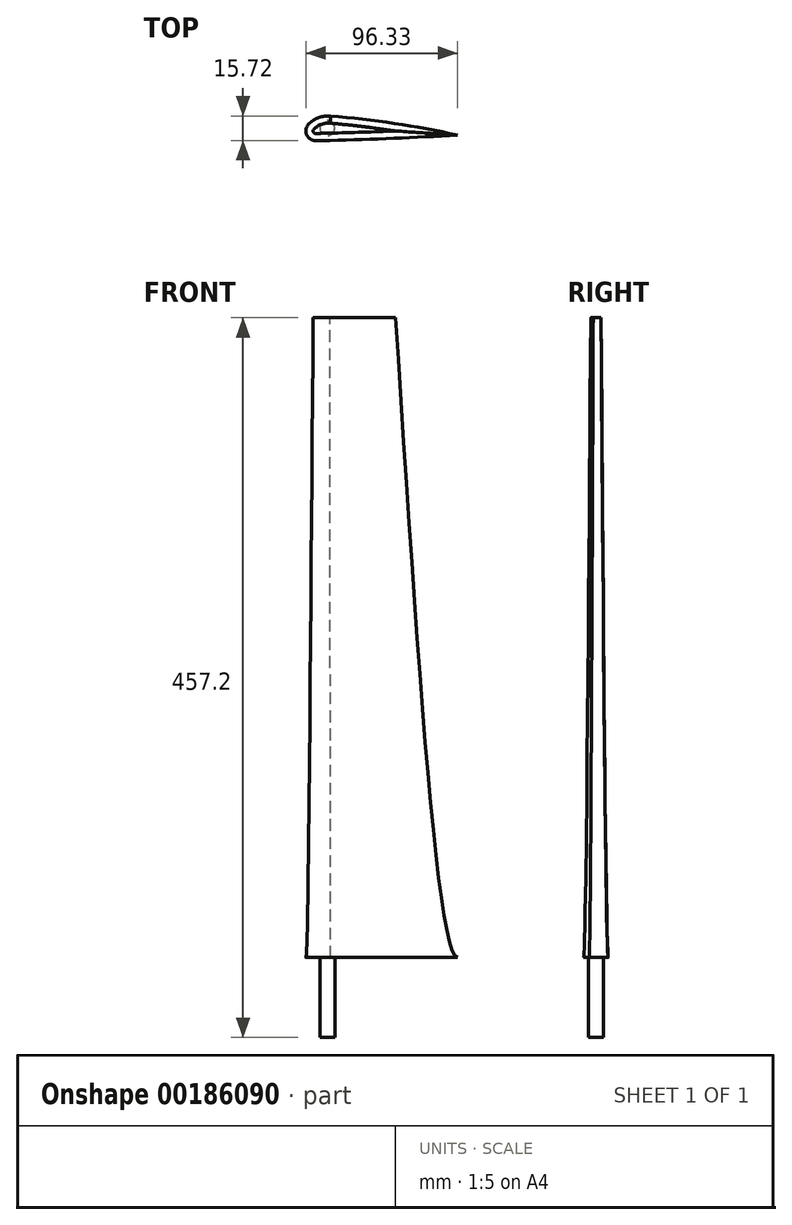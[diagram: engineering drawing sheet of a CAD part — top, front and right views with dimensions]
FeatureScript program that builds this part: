
annotation { "Feature Type Name" : "Feature", "Feature Type Description" : "" }
export const myFeature = defineFeature(function(context is Context, id is Id, definition is map)
    precondition{}
    {
        {
            var Q0;
            Q0=qCreatedBy(makeId("Top.planeOp"),FACE);
            cPlane(context, id + "F0", {"entities" : qUnion([Q0]), "cplaneType" : CPlaneType.OFFSET, "offset" : 101.6 * mm, "width" : 152.4 * mm, "height" : 152.4 * mm});
        }
        {
            var Q0;
            Q0=qCreatedBy(id+"F0.planeOp",FACE);
            cPlane(context, id + "F1", {"entities" : qUnion([Q0]), "cplaneType" : CPlaneType.OFFSET, "offset" : 101.6 * mm, "width" : 152.4 * mm, "height" : 152.4 * mm});
        }
        {
            var Q0;
            Q0=qCreatedBy(id+"F1.planeOp",FACE);
            cPlane(context, id + "F2", {"entities" : qUnion([Q0]), "cplaneType" : CPlaneType.OFFSET, "offset" : 101.6 * mm, "width" : 152.4 * mm, "height" : 152.4 * mm});
        }
        {
            var Q0;
            Q0=qCreatedBy(id+"F2.planeOp",FACE);
            cPlane(context, id + "F3", {"entities" : qUnion([Q0]), "cplaneType" : CPlaneType.OFFSET, "offset" : 101.6 * mm, "width" : 152.4 * mm, "height" : 152.4 * mm});
        }
        {
            var Q0;
            Q0=qCreatedBy(id+"F3.planeOp",FACE);
            var sketch = newSketch(context, id + "F4", { "sketchPlane" : qUnion([Q0])});
            skLineSegment(sketch, "E0", {"start": v(0, 0) * mm, "end": v(50.8, 0) * mm, "construction": true});
            skCircle(sketch, "E1", {"center": v(8.9, 1.78) * mm, "radius": 3.17 * mm, "construction": true});
            skArc(sketch, "E2", {"start": v(50.8, 0) * mm, "mid": v(30.02, 2.81) * mm, "end": v(9.16, 4.94) * mm});
            skArc(sketch, "E3", {"start": v(8.97, -1.4) * mm, "mid": v(29.89, -0.79) * mm, "end": v(50.8, 0) * mm});
            skCircle(sketch, "E4", {"center": v(0, 0) * mm, "radius": 1.59 * mm, "construction": true});
            skArc(sketch, "E5", {"start": v(9.16, 4.94) * mm, "mid": v(3.58, 4.18) * mm, "end": v(-1.14, 1.1) * mm});
            skArc(sketch, "E6", {"start": v(0.03, -1.59) * mm, "mid": v(4.5, -1.5) * mm, "end": v(8.97, -1.4) * mm});
            skArc(sketch, "E7", {"start": v(-1.14, 1.1) * mm, "mid": v(-1.46, -0.63) * mm, "end": v(0.03, -1.59) * mm});
            skSolve(sketch);
        }
        {
            var Q0;
            Q0=qCreatedBy(id+"F2.planeOp",FACE);
            var sketch = newSketch(context, id + "F5", { "sketchPlane" : qUnion([Q0])});
            skArc(sketch, "E8.0", {"start": v(9.27, 6.2) * mm, "mid": v(3.14, 5.37) * mm, "end": v(-2.05, 2) * mm});
            skArc(sketch, "E8.1", {"start": v(63.16, -0.72) * mm, "mid": v(36.29, 3.32) * mm, "end": v(9.27, 6.2) * mm});
            skArc(sketch, "E8.2", {"start": v(-2.05, 2) * mm, "mid": v(-2.62, -1.13) * mm, "end": v(0.05, -2.86) * mm});
            skArc(sketch, "E8.3", {"start": v(0.05, -2.86) * mm, "mid": v(4.53, -2.77) * mm, "end": v(9, -2.67) * mm});
            skArc(sketch, "E8.4", {"start": v(9, -2.67) * mm, "mid": v(36.08, -1.85) * mm, "end": v(63.16, -0.72) * mm});
            skSolve(sketch);
        }
        {
            var Q0;
            Q0=qCreatedBy(id+"F1.planeOp",FACE);
            var sketch = newSketch(context, id + "F6", { "sketchPlane" : qUnion([Q0])});
            skArc(sketch, "E9.0", {"start": v(9.33, 6.97) * mm, "mid": v(2.87, 6.08) * mm, "end": v(-2.6, 2.53) * mm});
            skArc(sketch, "E9.1", {"start": v(69.95, -1.15) * mm, "mid": v(39.74, 3.64) * mm, "end": v(9.33, 6.97) * mm});
            skArc(sketch, "E9.2", {"start": v(-2.6, 2.53) * mm, "mid": v(-3.32, -1.44) * mm, "end": v(0.07, -3.62) * mm});
            skArc(sketch, "E9.3", {"start": v(0.07, -3.62) * mm, "mid": v(4.54, -3.53) * mm, "end": v(9.02, -3.43) * mm});
            skArc(sketch, "E9.4", {"start": v(9.02, -3.43) * mm, "mid": v(39.49, -2.48) * mm, "end": v(69.95, -1.15) * mm});
            skSolve(sketch);
        }
        {
            var Q0;
            Q0=qCreatedBy(id+"F0.planeOp",FACE);
            var sketch = newSketch(context, id + "F7", { "sketchPlane" : qUnion([Q0])});
            skArc(sketch, "E10.0", {"start": v(9.44, 8.23) * mm, "mid": v(2.43, 7.27) * mm, "end": v(-3.5, 3.41) * mm});
            skArc(sketch, "E10.1", {"start": v(80.46, -1.87) * mm, "mid": v(45.1, 4.18) * mm, "end": v(9.44, 8.23) * mm});
            skArc(sketch, "E10.2", {"start": v(-3.5, 3.41) * mm, "mid": v(-4.49, -1.94) * mm, "end": v(0.09, -4.89) * mm});
            skArc(sketch, "E10.3", {"start": v(0.09, -4.89) * mm, "mid": v(4.57, -4.8) * mm, "end": v(9.05, -4.7) * mm});
            skArc(sketch, "E10.4", {"start": v(9.05, -4.7) * mm, "mid": v(44.76, -3.55) * mm, "end": v(80.46, -1.87) * mm});
            skSolve(sketch);
        }
        {
            var Q0;
            Q0=qCreatedBy(makeId("Top.planeOp"),FACE);
            var sketch = newSketch(context, id + "F8", { "sketchPlane" : qUnion([Q0])});
            skArc(sketch, "E11.0", {"start": v(9.55, 9.5) * mm, "mid": v(1.99, 8.46) * mm, "end": v(-4.4, 4.3) * mm});
            skArc(sketch, "E11.1", {"start": v(90.17, -2.6) * mm, "mid": v(50.05, 4.74) * mm, "end": v(9.55, 9.5) * mm});
            skArc(sketch, "E11.2", {"start": v(-4.4, 4.3) * mm, "mid": v(-5.65, -2.44) * mm, "end": v(0.11, -6.16) * mm});
            skArc(sketch, "E11.3", {"start": v(0.11, -6.16) * mm, "mid": v(4.6, -6.07) * mm, "end": v(9.08, -5.97) * mm});
            skArc(sketch, "E11.4", {"start": v(9.08, -5.97) * mm, "mid": v(49.64, -4.62) * mm, "end": v(90.17, -2.6) * mm});
            skSolve(sketch);
        }
        {
            var Q0;
            Q0=qCreatedBy(makeId("Front.planeOp"),FACE);
            var sketch = newSketch(context, id + "F9", { "sketchPlane" : qUnion([Q0])});
            skArc(sketch, "E12", {"start": v(90.17, 0) * mm, "mid": v(80.3, 204.15) * mm, "end": v(50.8, 406.4) * mm});
            skLineSegment(sketch, "E13", {"start": v(90.17, 0) * mm, "end": v(90.17, 413.58) * mm, "construction": true});
            skSolve(sketch);
        }
        {
            var Q0;
            Q0=makeQuery(id+"F8.imprint","IMPRINT",FACE,{"disambiguationData":[TD([[makeQuery(id+"F8.imprint","IMPRINT",EDGE,{"derivedFrom":sQuery(id+"F8.wireOp",EDGE,"E11.0")}),1.0]])]});
            var Q1;
            Q1=makeQuery(id+"F4.imprint","IMPRINT",FACE,{"disambiguationData":[TD([[makeQuery(id+"F4.imprint","IMPRINT",EDGE,{"derivedFrom":sQuery(id+"F4.wireOp",EDGE,"E2")}),1.0]])]});
            var Q2;
            Q2=sQuery(id+"F9.wireOp",EDGE,"E12");
            loft(context, id + "F10", {"startCondition" : LoftEndDerivativeType.TANGENT_TO_PROFILE, "startMagnitude" : 1, "sheetProfilesArray" : [{ "sheetProfileEntities" : qUnion([Q0]) }, { "sheetProfileEntities" : qUnion([Q1]) }], "guidesArray" : [{ "guideEntities" : qUnion([Q2]), "guideDerivativeType" : LoftGuideDerivativeType.DEFAULT, "guideDerivativeMagnitude" : 1 }]});
        }
        {
            var Q0;
            Q0=makeQuery(id+"F10.opLoft","CAP_FACE",FACE,{"disambiguationData":[OSD([makeQuery(id+"F8.imprint","IMPRINT",FACE,{"disambiguationData":[TD([[makeQuery(id+"F8.imprint","IMPRINT",EDGE,{"derivedFrom":sQuery(id+"F8.wireOp",EDGE,"E11.0")}),1.0]])]})])],"isStart":true});
            var sketch = newSketch(context, id + "F11", { "sketchPlane" : qUnion([Q0])});
            skCircle(sketch, "E14", {"center": v(7.4, -1.82) * mm, "radius": 4.76 * mm});
            skSolve(sketch);
        }
        {
            var Q0;
            Q0 = qSketchRegion(id + "F11", true);
            extrude(context, id + "F12", {"entities" : qUnion([Q0]), "depth" : 50.8 * mm});
        }
    });
